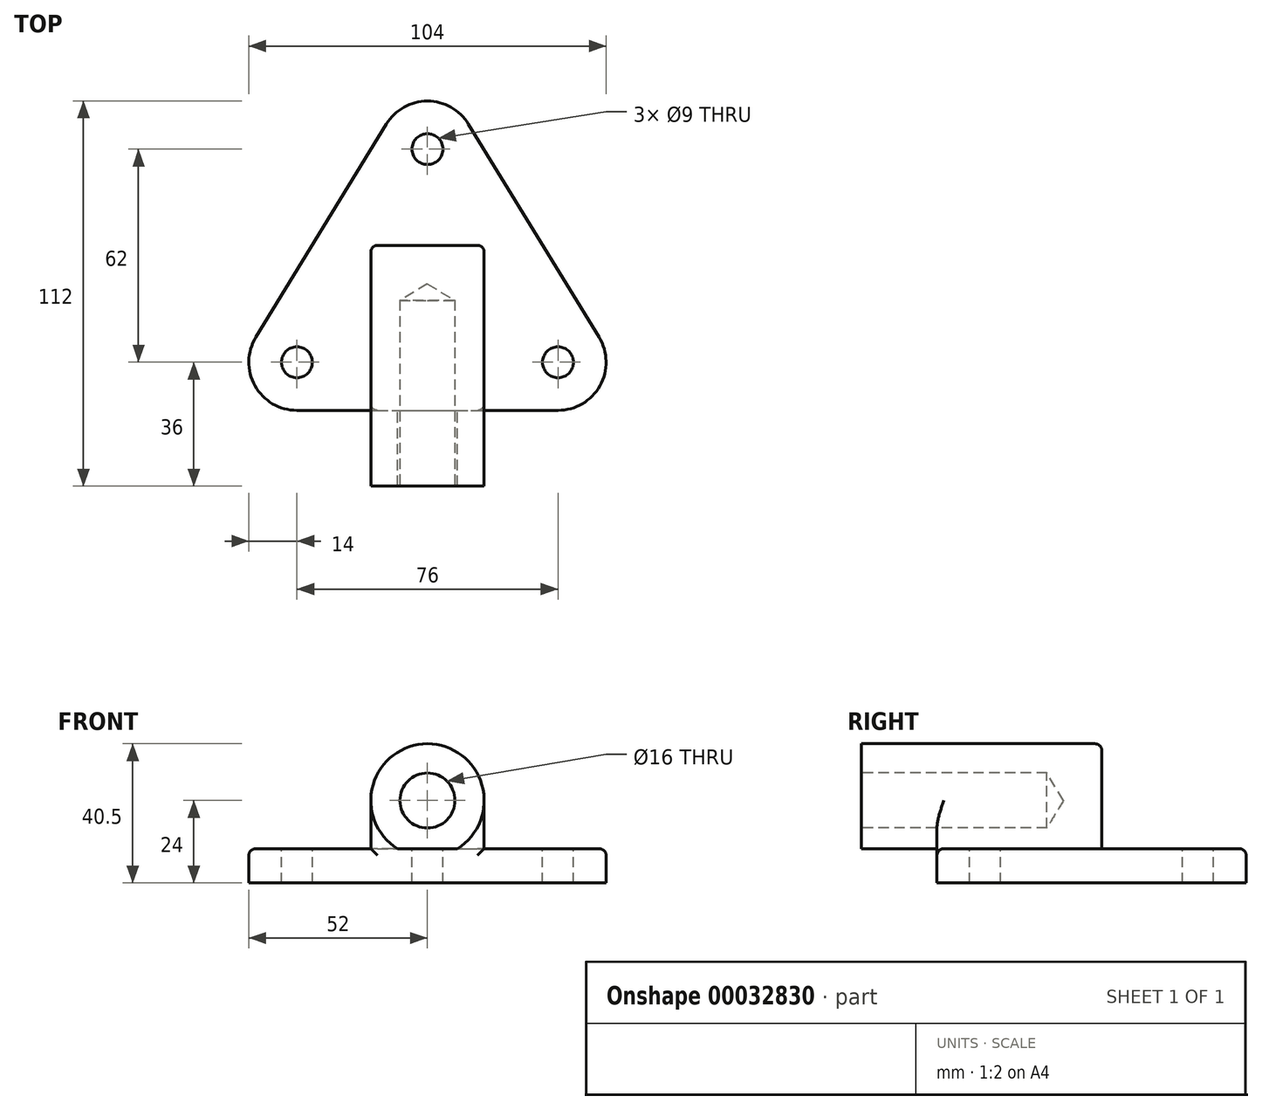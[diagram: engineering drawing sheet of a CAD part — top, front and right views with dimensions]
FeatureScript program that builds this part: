
annotation { "Feature Type Name" : "Feature", "Feature Type Description" : "" }
export const myFeature = defineFeature(function(context is Context, id is Id, definition is map)
    precondition{}
    {
        {
            var Q0;
            Q0=qCreatedBy(makeId("Top.planeOp"),FACE);
            var sketch = newSketch(context, id + "F0", { "sketchPlane" : qUnion([Q0])});
            skCircle(sketch, "E0", {"center": v(0, 0) * mm, "radius": 14 * mm});
            skCircle(sketch, "E1", {"center": v(-38, -62) * mm, "radius": 14 * mm});
            skCircle(sketch, "E2", {"center": v(38, -62) * mm, "radius": 14 * mm});
            skLineSegment(sketch, "E3", {"start": v(-38, -62) * mm, "end": v(38, -62) * mm, "construction": true});
            skLineSegment(sketch, "E4", {"start": v(0, -62) * mm, "end": v(0, 0) * mm, "construction": true});
            skLineSegment(sketch, "E5", {"start": v(-11.94, 7.32) * mm, "end": v(-49.94, -54.68) * mm});
            skLineSegment(sketch, "E6", {"start": v(-38, -76) * mm, "end": v(38, -76) * mm});
            skLineSegment(sketch, "E7", {"start": v(11.94, 7.32) * mm, "end": v(49.94, -54.68) * mm});
            skSolve(sketch);
        }
        {
            var Q0;
            {var subQ2=sQuery(id+"F0.wireOp",EDGE,"E5");Q0=makeQuery(id+"F0.imprint","IMPRINT",FACE,{"disambiguationData":[TD([[makeQuery(id+"F0.imprint","IMPRINT",EDGE,{"derivedFrom":subQ2}),1.0]])]});}
            var Q1;
            {var subQ0=sQuery(id+"F0.wireOp",EDGE,"E1");var subQ2=makeQuery(id+"F0.imprint","INTERSECT",VERTEX,{"derivedFrom":[subQ0,sQuery(id+"F0.wireOp",EDGE,"E5")]});Q1=makeQuery(id+"F0.imprint","IMPRINT",FACE,{"disambiguationData":[TD([[makeQuery(id+"F0.imprint","IMPRINT",EDGE,{"disambiguationData":[TD([[subQ2,-1.0]])],"derivedFrom":subQ0}),1.0]])]});}
            var Q2;
            {var subQ0=sQuery(id+"F0.wireOp",EDGE,"E0");var subQ2=makeQuery(id+"F0.imprint","INTERSECT",VERTEX,{"derivedFrom":[subQ0,sQuery(id+"F0.wireOp",EDGE,"E5")]});Q2=makeQuery(id+"F0.imprint","IMPRINT",FACE,{"disambiguationData":[TD([[makeQuery(id+"F0.imprint","IMPRINT",EDGE,{"disambiguationData":[TD([[subQ2,1.0]])],"derivedFrom":subQ0}),1.0]])]});}
            var Q3;
            {var subQ0=sQuery(id+"F0.wireOp",EDGE,"E2");var subQ2=makeQuery(id+"F0.imprint","INTERSECT",VERTEX,{"derivedFrom":[subQ0,sQuery(id+"F0.wireOp",EDGE,"E6")]});Q3=makeQuery(id+"F0.imprint","IMPRINT",FACE,{"disambiguationData":[TD([[makeQuery(id+"F0.imprint","IMPRINT",EDGE,{"disambiguationData":[TD([[subQ2,1.0]])],"derivedFrom":subQ0}),1.0]])]});}
            extrude(context, id + "F1", {"entities" : qUnion([Q0, Q1, Q2, Q3]), "depth" : 10 * mm});
        }
        {
            var Q0;
            Q0=makeQuery(id+"F1.opExtrude","SWEPT_FACE",FACE,{"disambiguationData":[OSD([sQuery(id+"F0.wireOp",EDGE,"E6")])]});
            var sketch = newSketch(context, id + "F2", { "sketchPlane" : qUnion([Q0])});
            skCircle(sketch, "E8", {"center": v(0, 24) * mm, "radius": 16.5 * mm});
            skPoint(sketch, "E8.centerSnap0", {"position": v(0, 10) * mm});
            skLineSegment(sketch, "E9", {"start": v(16.5, 24) * mm, "end": v(16.5, 10) * mm});
            skLineSegment(sketch, "E10", {"start": v(-16.5, 24) * mm, "end": v(-16.5, 10) * mm});
            skSolve(sketch);
        }
        {
            var Q0;
            {var subQ1=sQuery(id+"F2.wireOp",EDGE,"E8");var subQ4=makeQuery(id+"F2.imprint","INTERSECT",VERTEX,{"derivedFrom":[subQ1,sQuery(id+"F2.wireOp",EDGE,"E9")]});Q0=makeQuery(id+"F2.imprint","IMPRINT",FACE,{"disambiguationData":[TD([[makeQuery(id+"F2.imprint","IMPRINT",EDGE,{"disambiguationData":[TD([[subQ4,-1.0]])],"derivedFrom":subQ1}),1.0]])]});}
            var Q1;
            {var subQ0=makeQuery(id+"F1.opExtrude","CAP_EDGE",EDGE,{"disambiguationData":[OSD([sQuery(id+"F0.wireOp",EDGE,"E6")])],"isStart":false});var subQ1=sQuery(id+"F2.wireOp",EDGE,"E8");var subQ3=makeQuery(id+"F2.imprint","INTERSECT",VERTEX,{"disambiguationData":[OD(0.0)],"derivedFrom":[subQ0,subQ1]});Q1=makeQuery(id+"F2.imprint","IMPRINT",FACE,{"disambiguationData":[TD([[makeQuery(id+"F2.imprint","IMPRINT",EDGE,{"disambiguationData":[TD([[subQ3,-1.0]])],"derivedFrom":subQ1}),1.0]])]});}
            extrude(context, id + "F3", {"entities" : qUnion([Q0, Q1]), "operationType" : NewBodyOperationType.ADD, "depth" : 22 * mm});
        }
        {
            var Q0;
            {var subQ3=sQuery(id+"F2.wireOp",EDGE,"E9");Q0=makeQuery(id+"F2.imprint","IMPRINT",FACE,{"disambiguationData":[TD([[makeQuery(id+"F2.imprint","IMPRINT",EDGE,{"derivedFrom":subQ3}),-1.0]])]});}
            var Q1;
            {var subQ1=sQuery(id+"F2.wireOp",EDGE,"E8");var subQ4=makeQuery(id+"F2.imprint","INTERSECT",VERTEX,{"derivedFrom":[subQ1,sQuery(id+"F2.wireOp",EDGE,"E9")]});Q1=makeQuery(id+"F2.imprint","IMPRINT",FACE,{"disambiguationData":[TD([[makeQuery(id+"F2.imprint","IMPRINT",EDGE,{"disambiguationData":[TD([[subQ4,-1.0]])],"derivedFrom":subQ1}),1.0]])]});}
            var Q2;
            {var subQ3=sQuery(id+"F2.wireOp",EDGE,"E10");Q2=makeQuery(id+"F2.imprint","IMPRINT",FACE,{"disambiguationData":[TD([[makeQuery(id+"F2.imprint","IMPRINT",EDGE,{"derivedFrom":subQ3}),1.0]])]});}
            extrude(context, id + "F4", {"entities" : qUnion([Q0, Q1, Q2]), "operationType" : NewBodyOperationType.ADD, "oppositeDirection" : true, "depth" : 48 * mm});
        }
        {
            var Q0;
            Q0=makeQuery(id+"F3.opExtrude","CAP_FACE",FACE,{"disambiguationData":[OSD([sQuery(id+"F2.wireOp",EDGE,"E8")])],"isStart":false});
            var sketch = newSketch(context, id + "F5", { "sketchPlane" : qUnion([Q0])});
            skPoint(sketch, "E11", {"position": v(0, 24) * mm});
            skSolve(sketch);
        }
        {
            var Q0;
            Q0=sQuery(id+"F5.wireOp",VERTEX,"E11");
            var Q1;
            Q1=makeQuery(id+"F1.opExtrude","SWEPT_BODY",BODY,{"disambiguationData":[OSD([sQuery(id+"F0.wireOp",EDGE,"E0"),sQuery(id+"F0.wireOp",EDGE,"E1"),sQuery(id+"F0.wireOp",EDGE,"E2"),sQuery(id+"F0.wireOp",EDGE,"E5"),sQuery(id+"F0.wireOp",EDGE,"E6"),sQuery(id+"F0.wireOp",EDGE,"E7")])]});
            hole(context, id + "F6", {"style" : HoleStyle.SIMPLE, "holeDiameter" : 16 * mm, "endStyle" : HoleEndStyle.BLIND, "holeDepth" : 54 * mm, "locations" : qUnion([Q0]), "scope" : qUnion([Q1])});
        }
        {
            var Q0;
            Q0=makeQuery(id+"F1.opExtrude","CAP_EDGE",EDGE,{"disambiguationData":[OSD([sQuery(id+"F0.wireOp",EDGE,"E2")])],"isStart":false});
            var Q1;
            Q1=makeQuery(id+"F4.opExtrude","CAP_EDGE",EDGE,{"disambiguationData":[OSD([sQuery(id+"F2.wireOp",EDGE,"E8")])],"isStart":false});
            var Q2;
            Q2=makeQuery(id+"F4.opExtrude","SWEPT_EDGE",EDGE,{"disambiguationData":[OSD([sQuery(id+"F0.wireOp",EDGE,"E6"),sQuery(id+"F2.wireOp",EDGE,"E9")])]});
            var Q3;
            Q3=makeQuery(id+"F4.opExtrude","CAP_EDGE",EDGE,{"disambiguationData":[OSD([sQuery(id+"F2.wireOp",EDGE,"E9")])],"isStart":true});
            var Q4;
            Q4=makeQuery(id+"F4.opExtrude","CAP_EDGE",EDGE,{"disambiguationData":[OSD([sQuery(id+"F2.wireOp",EDGE,"E10")])],"isStart":true});
            fillet(context, id + "F7", {"entities" : qUnion([Q0, Q1, Q2, Q3, Q4]), "radius" : 2 * mm, "tangentPropagation" : true, "allowEdgeOverflow" : false});
        }
        {
            var Q0;
            Q0=makeQuery(id+"F1.opExtrude","CAP_FACE",FACE,{"disambiguationData":[OSD([sQuery(id+"F0.wireOp",EDGE,"E0"),sQuery(id+"F0.wireOp",EDGE,"E1"),sQuery(id+"F0.wireOp",EDGE,"E2"),sQuery(id+"F0.wireOp",EDGE,"E5"),sQuery(id+"F0.wireOp",EDGE,"E6"),sQuery(id+"F0.wireOp",EDGE,"E7")])],"isStart":false});
            var sketch = newSketch(context, id + "F8", { "sketchPlane" : qUnion([Q0])});
            skPoint(sketch, "E12", {"position": v(-38, -62) * mm});
            skPoint(sketch, "E13", {"position": v(38, -62) * mm});
            skPoint(sketch, "E14", {"position": v(0, 0) * mm});
            skSolve(sketch);
        }
        {
            var Q0;
            Q0=sQuery(id+"F8.wireOp",VERTEX,"E13");
            var Q1;
            Q1=sQuery(id+"F8.wireOp",VERTEX,"E14");
            var Q2;
            Q2=sQuery(id+"F8.wireOp",VERTEX,"E12");
            var Q3;
            Q3=makeQuery(id+"F1.opExtrude","SWEPT_BODY",BODY,{"disambiguationData":[OSD([sQuery(id+"F0.wireOp",EDGE,"E0"),sQuery(id+"F0.wireOp",EDGE,"E1"),sQuery(id+"F0.wireOp",EDGE,"E2"),sQuery(id+"F0.wireOp",EDGE,"E5"),sQuery(id+"F0.wireOp",EDGE,"E6"),sQuery(id+"F0.wireOp",EDGE,"E7")])]});
            hole(context, id + "F9", {"style" : HoleStyle.SIMPLE, "holeDiameter" : 9 * mm, "endStyle" : HoleEndStyle.THROUGH, "locations" : qUnion([Q0, Q1, Q2]), "scope" : qUnion([Q3])});
        }
    });
